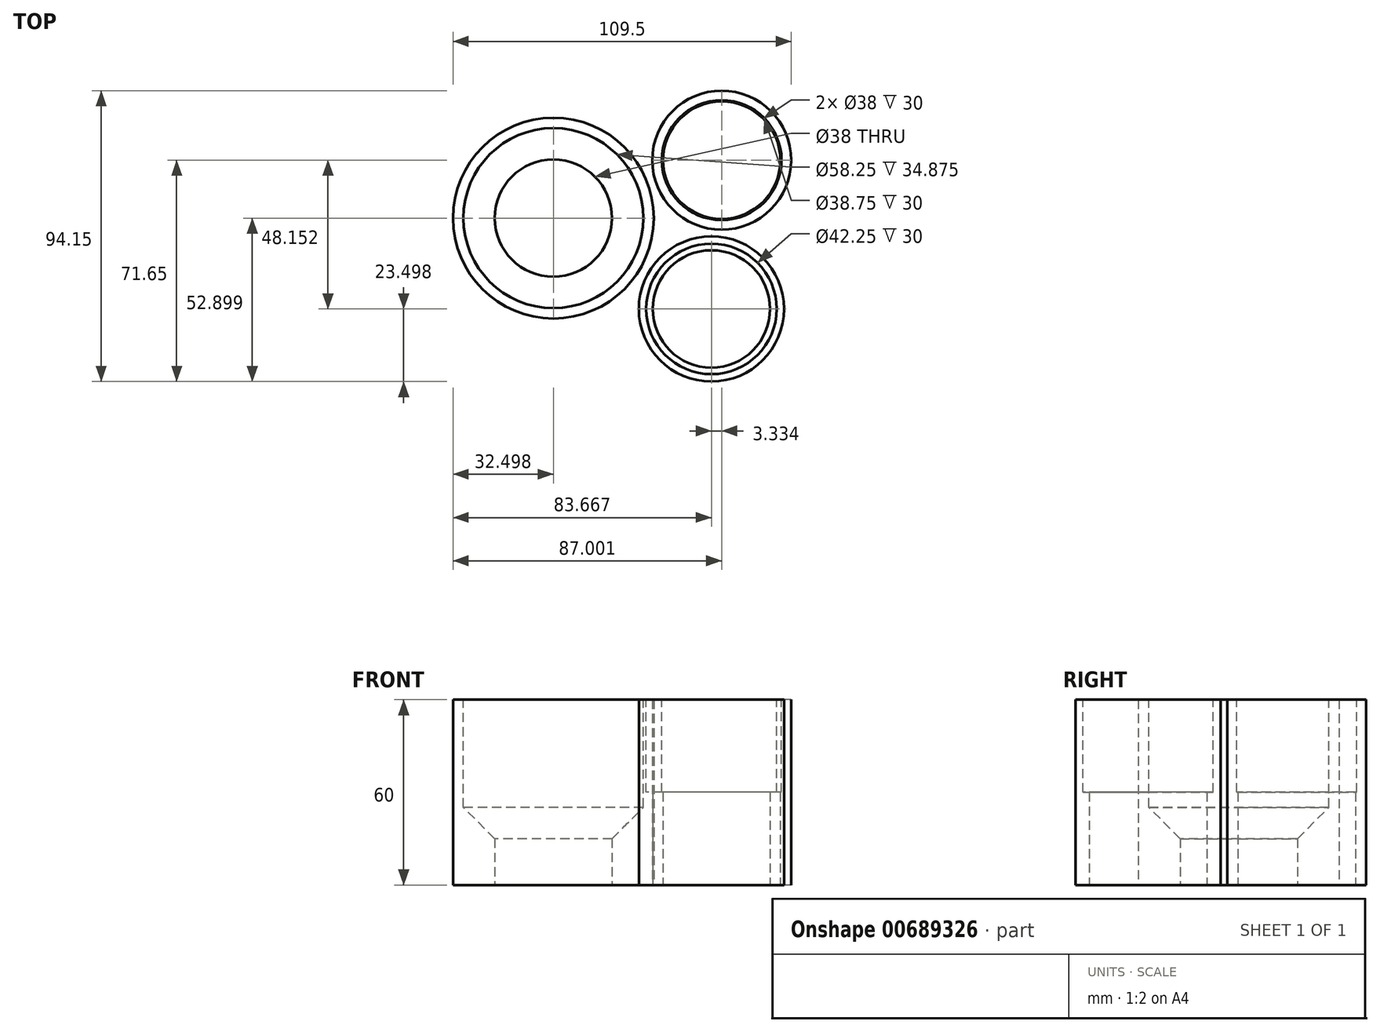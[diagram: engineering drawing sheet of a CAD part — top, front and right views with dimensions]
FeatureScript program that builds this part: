
annotation { "Feature Type Name" : "Feature", "Feature Type Description" : "" }
export const myFeature = defineFeature(function(context is Context, id is Id, definition is map)
    precondition{}
    {
        {
            var Q0;
            Q0=qCreatedBy(makeId("Top.planeOp"),FACE);
            var sketch = newSketch(context, id + "F0", { "sketchPlane" : qUnion([Q0])});
            skCircle(sketch, "E0", {"center": v(-29.25, 19.27) * mm, "radius": 32.5 * mm});
            skCircle(sketch, "E1", {"center": v(25.25, 38.02) * mm, "radius": 22.5 * mm});
            skCircle(sketch, "E2", {"center": v(21.92, -10.13) * mm, "radius": 23.5 * mm});
            skSolve(sketch);
        }
        {
            var Q0;
            Q0 = qSketchRegion(id + "F0", true);
            extrude(context, id + "F1", {"entities" : qUnion([Q0]), "depth" : 60 * mm, "offsetDistance" : 25 * mm});
        }
        {
            var Q0;
            Q0=qCreatedBy(makeId("Top.planeOp"),FACE);
            var sketch = newSketch(context, id + "F2", { "sketchPlane" : qUnion([Q0])});
            skCircle(sketch, "E3.0", {"center": v(-29.25, 19.27) * mm, "radius": 32.5 * mm, "construction": true});
            skCircle(sketch, "E4", {"center": v(-29.25, 19.27) * mm, "radius": 19 * mm});
            skCircle(sketch, "E5.0", {"center": v(25.25, 38.02) * mm, "radius": 22.5 * mm, "construction": true});
            skCircle(sketch, "E6", {"center": v(25.25, 38.02) * mm, "radius": 19 * mm});
            skCircle(sketch, "E7.0", {"center": v(21.92, -10.13) * mm, "radius": 23.5 * mm, "construction": true});
            skCircle(sketch, "E8", {"center": v(21.92, -10.13) * mm, "radius": 19 * mm});
            skSolve(sketch);
        }
        {
            var Q0;
            Q0 = qSketchRegion(id + "F2", true);
            var Q1;
            Q1=makeQuery(id+"F1.opExtrude","CAP_FACE",FACE,{"disambiguationData":[OSD([sQuery(id+"F0.wireOp",EDGE,"E0")])],"isStart":false});
            extrude(context, id + "F3", {"entities" : qUnion([Q0]), "operationType" : NewBodyOperationType.REMOVE, "endBound" : BoundingType.UP_TO_SURFACE, "depth" : 25 * mm, "endBoundEntityFace" : qUnion([Q1]), "offsetDistance" : 25 * mm});
        }
        {
            var Q0;
            Q0=makeQuery(id+"F1.opExtrude","CAP_FACE",FACE,{"disambiguationData":[OSD([sQuery(id+"F0.wireOp",EDGE,"E0")])],"isStart":false});
            cPlane(context, id + "F4", {"entities" : qUnion([Q0]), "cplaneType" : CPlaneType.OFFSET, "offset" : 0 * mm, "width" : 150 * mm, "height" : 150 * mm});
        }
        {
            var Q0;
            Q0=qCreatedBy(id+"F4.planeOp",FACE);
            var sketch = newSketch(context, id + "F5", { "sketchPlane" : qUnion([Q0])});
            skCircle(sketch, "E9.0", {"center": v(-29.25, 19.27) * mm, "radius": 32.5 * mm, "construction": true});
            skCircle(sketch, "E10", {"center": v(-29.25, 19.27) * mm, "radius": 29.12 * mm});
            skCircle(sketch, "E11.0", {"center": v(25.25, 38.02) * mm, "radius": 22.5 * mm, "construction": true});
            skCircle(sketch, "E12", {"center": v(25.25, 38.02) * mm, "radius": 19.38 * mm});
            skCircle(sketch, "E13.0", {"center": v(21.92, -10.13) * mm, "radius": 23.5 * mm, "construction": true});
            skCircle(sketch, "E14", {"center": v(21.92, -10.13) * mm, "radius": 21.12 * mm});
            skSolve(sketch);
        }
        {
            var Q0;
            Q0 = qSketchRegion(id + "F5", true);
            extrude(context, id + "F6", {"entities" : qUnion([Q0]), "operationType" : NewBodyOperationType.REMOVE, "oppositeDirection" : true, "depth" : 30 * mm, "offsetDistance" : 25 * mm});
        }
        {
            var Q0;
            Q0=makeQuery(id+"F6.boolean.opBoolean","INTERSECT",EDGE,{"derivedFrom":[makeQuery(id+"F3.boolean.opBoolean","COPY",FACE,{"derivedFrom":makeQuery(id+"F3.opExtrude","SWEPT_FACE",FACE,{"disambiguationData":[OSD([sQuery(id+"F2.wireOp",EDGE,"E4")])]})}),makeQuery(id+"F6.opExtrude","CAP_FACE",FACE,{"disambiguationData":[OSD([sQuery(id+"F5.wireOp",EDGE,"E10")])],"isStart":false})]});
            chamfer(context, id + "F7", {"entities" : qUnion([Q0]), "width" : 15 * mm, "tangentPropagation" : true});
        }
    });
